# Revit family: Sanitary_Showers_AXOR_35372USA-AXOR-ShowerSolutions-Overhead-s_876
name_source: partatom
category: Generic Models
revit_build: Autodesk Revit 2018 (Build: 20170223_1515(x64)
units: mm (PartAtom-declared; Revit-internal decimal feet)

## family parameters
Always vertical = No
Can host rebar = No
Cut with Voids When Loaded = No
OmniClass Number = 23.31.17.19
OmniClass Title = Shower Head Fixtures
Part Type = Normal
Room Calculation Point = No
Round Connector Dimension = Use Diameter
Shared = No
Work Plane-Based = No

## types (7) — shared parameters
BIMobject category = Showers
Description = AXOR ShowerSolutions Overhead shower 230/180 1jet 1.5 GPM
Design country = Germany
Edition number = 1
IFC Classification = Sanitary Terminal
Installation instructions = https://www.axor-design.com
Manufacturer = AXOR
Manufacturer country = Germany
Manufacturer name = AXOR
Model = 35372USA
OmniClass Code = 23-31 17 19
OmniClass Description = Shower Head Fixtures
Product Guid = 3b5a6e48-8a8f-4400-879b-72b80090a203
Product SKU = 35372USA
Product data url = https://bimobject.com
Product family = AXOR ShowerSolutions
Product group = Overhead showers
Product name = 35372USA AXOR ShowerSolutions Overhead shower 230/180 1jet 1.5 GPM
Product url = https://www.axor-design.com
QR code = https://bimobject.com
URL = https://www.axor-design.com
Water Inlet = 13 mm
Water Inlet Description = Water Inlet 12.7mm
Weight Net (Kg) = 1,9

## per-type parameters (varying)
| type | Material 1 |
| 001 Chrome | AXOR - Metal - 001 Chrome |
| 251 Brushed Gold Optic | AXOR - Metal - 251 Brushed Gold Optic |
| 331 Polished Black Chrome | AXOR - Metal - 331 Polished Black Chrome |
| 341 Brushed Black Chrome | AXOR - Metal - 341 Brushed Black Chrome |
| 671 Matt Black | AXOR - Metal - 671 Matt Black |
| 821 Brushed Nickel | AXOR - Metal - 821 Brushed Nickel |
| 991 Polished Gold Optic | AXOR - Metal - 991 Polished Gold Optic |

## geometry (parser evidence)
native form markers: Sweep x2
no freeform markers — native parametric forms only
